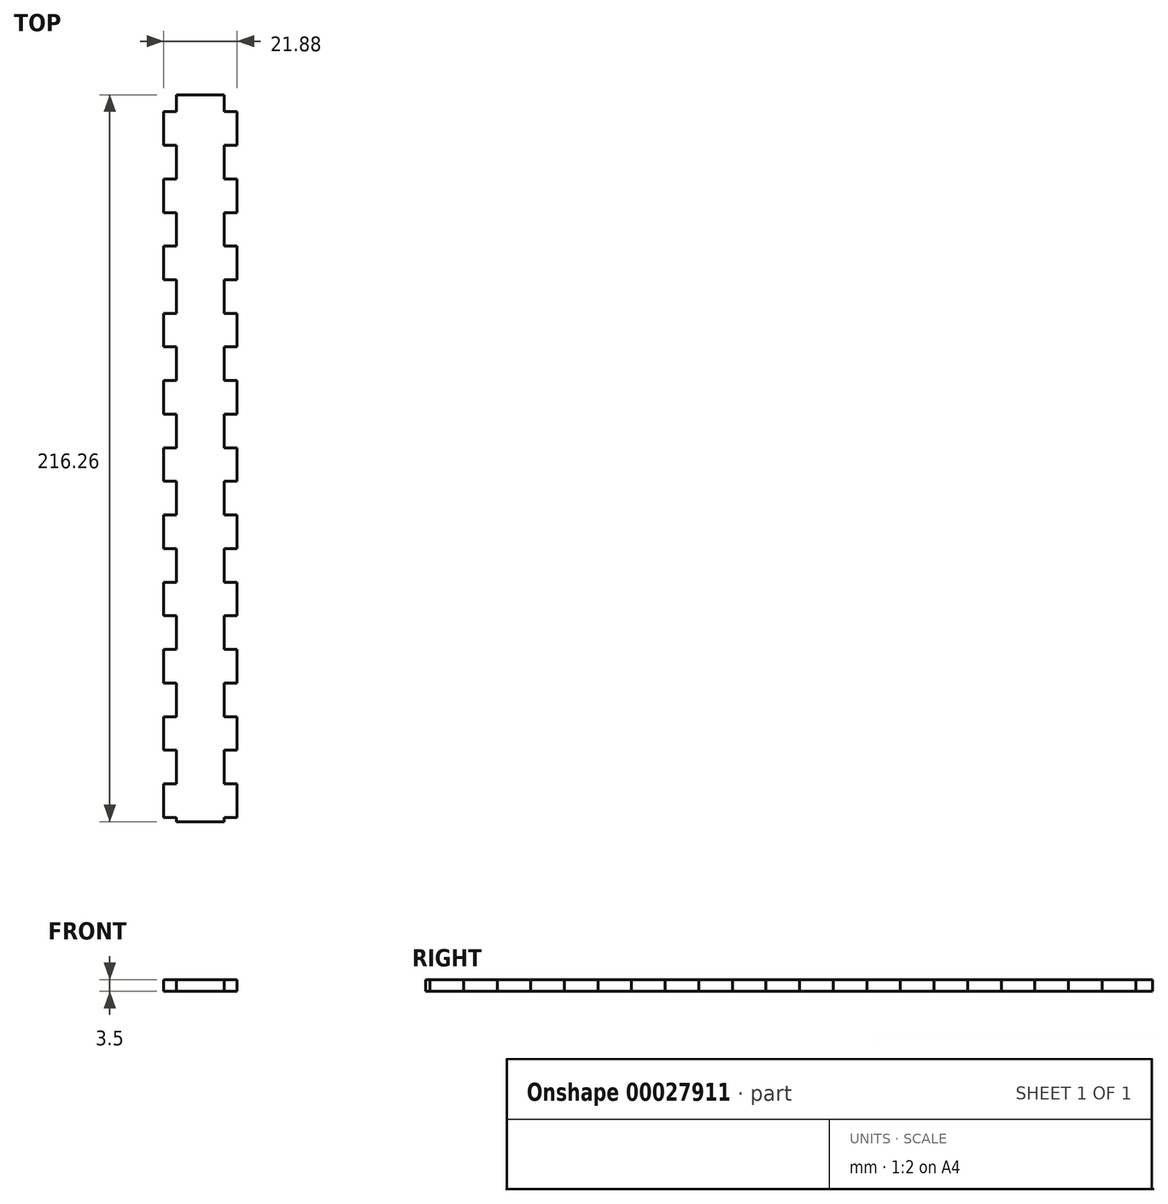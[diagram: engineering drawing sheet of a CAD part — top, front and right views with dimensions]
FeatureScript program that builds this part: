
annotation { "Feature Type Name" : "Feature", "Feature Type Description" : "" }
export const myFeature = defineFeature(function(context is Context, id is Id, definition is map)
    precondition{}
    {
        {
            var Q0;
            Q0=qCreatedBy(makeId("Top.planeOp"),FACE);
            var sketch = newSketch(context, id + "F0", { "sketchPlane" : qUnion([Q0])});
            skLineSegment(sketch, "E0.rect.bottom", {"start": v(7.14, -108.13) * mm, "end": v(-7.14, -108.13) * mm});
            skLineSegment(sketch, "E0.rect.top", {"start": v(7.14, 108.13) * mm, "end": v(-7.14, 108.13) * mm});
            skPoint(sketch, "E0.rect.middle", {"position": v(0, 0) * mm});
            skLineSegment(sketch, "E1", {"start": v(7.14, 108.13) * mm, "end": v(7.14, 103.13) * mm});
            skLineSegment(sketch, "E2.bottom", {"start": v(7.14, 103.13) * mm, "end": v(10.94, 103.13) * mm});
            skLineSegment(sketch, "E2.top", {"start": v(7.14, 93.13) * mm, "end": v(10.94, 93.13) * mm});
            skLineSegment(sketch, "E2.right", {"start": v(10.94, 103.13) * mm, "end": v(10.94, 93.13) * mm});
            skLineSegment(sketch, "E3", {"start": v(7.14, 93.13) * mm, "end": v(7.14, 88.13) * mm});
            skLineSegment(sketch, "E4.0.1.0", {"start": v(7.14, 88.13) * mm, "end": v(7.14, 83.13) * mm});
            skLineSegment(sketch, "E4.0.1.1", {"start": v(7.14, 83.13) * mm, "end": v(10.94, 83.13) * mm});
            skLineSegment(sketch, "E4.0.1.2", {"start": v(10.94, 83.13) * mm, "end": v(10.94, 73.13) * mm});
            skLineSegment(sketch, "E4.0.1.3", {"start": v(7.14, 73.13) * mm, "end": v(10.94, 73.13) * mm});
            skLineSegment(sketch, "E4.0.1.4", {"start": v(7.14, 73.13) * mm, "end": v(7.14, 68.13) * mm});
            skLineSegment(sketch, "E4.0.2.0", {"start": v(7.14, 68.13) * mm, "end": v(7.14, 63.13) * mm});
            skLineSegment(sketch, "E4.0.2.1", {"start": v(7.14, 63.13) * mm, "end": v(10.94, 63.13) * mm});
            skLineSegment(sketch, "E4.0.2.2", {"start": v(10.94, 63.13) * mm, "end": v(10.94, 53.13) * mm});
            skLineSegment(sketch, "E4.0.2.3", {"start": v(7.14, 53.13) * mm, "end": v(10.94, 53.13) * mm});
            skLineSegment(sketch, "E4.0.2.4", {"start": v(7.14, 53.13) * mm, "end": v(7.14, 48.13) * mm});
            skLineSegment(sketch, "E4.0.3.0", {"start": v(7.14, 48.13) * mm, "end": v(7.14, 43.13) * mm});
            skLineSegment(sketch, "E4.0.3.1", {"start": v(7.14, 43.13) * mm, "end": v(10.94, 43.13) * mm});
            skLineSegment(sketch, "E4.0.3.2", {"start": v(10.94, 43.13) * mm, "end": v(10.94, 33.13) * mm});
            skLineSegment(sketch, "E4.0.3.3", {"start": v(7.14, 33.13) * mm, "end": v(10.94, 33.13) * mm});
            skLineSegment(sketch, "E4.0.3.4", {"start": v(7.14, 33.13) * mm, "end": v(7.14, 28.13) * mm});
            skLineSegment(sketch, "E4.0.4.0", {"start": v(7.14, 28.13) * mm, "end": v(7.14, 23.13) * mm});
            skLineSegment(sketch, "E4.0.4.1", {"start": v(7.14, 23.13) * mm, "end": v(10.94, 23.13) * mm});
            skLineSegment(sketch, "E4.0.4.2", {"start": v(10.94, 23.13) * mm, "end": v(10.94, 13.13) * mm});
            skLineSegment(sketch, "E4.0.4.3", {"start": v(7.14, 13.13) * mm, "end": v(10.94, 13.13) * mm});
            skLineSegment(sketch, "E4.0.4.4", {"start": v(7.14, 13.13) * mm, "end": v(7.14, 8.13) * mm});
            skLineSegment(sketch, "E4.0.5.0", {"start": v(7.14, 8.13) * mm, "end": v(7.14, 3.13) * mm});
            skLineSegment(sketch, "E4.0.5.1", {"start": v(7.14, 3.13) * mm, "end": v(10.94, 3.13) * mm});
            skLineSegment(sketch, "E4.0.5.2", {"start": v(10.94, 3.13) * mm, "end": v(10.94, -6.87) * mm});
            skLineSegment(sketch, "E4.0.5.3", {"start": v(7.14, -6.87) * mm, "end": v(10.94, -6.87) * mm});
            skLineSegment(sketch, "E4.0.5.4", {"start": v(7.14, -6.87) * mm, "end": v(7.14, -11.87) * mm});
            skLineSegment(sketch, "E4.0.6.0", {"start": v(7.14, -11.87) * mm, "end": v(7.14, -16.87) * mm});
            skLineSegment(sketch, "E4.0.6.1", {"start": v(7.14, -16.87) * mm, "end": v(10.94, -16.87) * mm});
            skLineSegment(sketch, "E4.0.6.2", {"start": v(10.94, -16.87) * mm, "end": v(10.94, -26.87) * mm});
            skLineSegment(sketch, "E4.0.6.3", {"start": v(7.14, -26.87) * mm, "end": v(10.94, -26.87) * mm});
            skLineSegment(sketch, "E4.0.6.4", {"start": v(7.14, -26.87) * mm, "end": v(7.14, -31.87) * mm});
            skLineSegment(sketch, "E4.0.7.0", {"start": v(7.14, -31.87) * mm, "end": v(7.14, -36.87) * mm});
            skLineSegment(sketch, "E4.0.7.1", {"start": v(7.14, -36.87) * mm, "end": v(10.94, -36.87) * mm});
            skLineSegment(sketch, "E4.0.7.2", {"start": v(10.94, -36.87) * mm, "end": v(10.94, -46.87) * mm});
            skLineSegment(sketch, "E4.0.7.3", {"start": v(7.14, -46.87) * mm, "end": v(10.94, -46.87) * mm});
            skLineSegment(sketch, "E4.0.7.4", {"start": v(7.14, -46.87) * mm, "end": v(7.14, -51.87) * mm});
            skLineSegment(sketch, "E4.0.8.0", {"start": v(7.14, -51.87) * mm, "end": v(7.14, -56.87) * mm});
            skLineSegment(sketch, "E4.0.8.1", {"start": v(7.14, -56.87) * mm, "end": v(10.94, -56.87) * mm});
            skLineSegment(sketch, "E4.0.8.2", {"start": v(10.94, -56.87) * mm, "end": v(10.94, -66.87) * mm});
            skLineSegment(sketch, "E4.0.8.3", {"start": v(7.14, -66.87) * mm, "end": v(10.94, -66.87) * mm});
            skLineSegment(sketch, "E4.0.8.4", {"start": v(7.14, -66.87) * mm, "end": v(7.14, -71.87) * mm});
            skLineSegment(sketch, "E4.0.9.0", {"start": v(7.14, -71.87) * mm, "end": v(7.14, -76.87) * mm});
            skLineSegment(sketch, "E4.0.9.4", {"start": v(7.14, -86.87) * mm, "end": v(7.14, -91.87) * mm});
            skLineSegment(sketch, "E4.0.10.0", {"start": v(7.14, -91.87) * mm, "end": v(7.14, -96.87) * mm});
            skLineSegment(sketch, "E4.0.10.1", {"start": v(7.14, -96.87) * mm, "end": v(10.94, -96.87) * mm});
            skLineSegment(sketch, "E4.0.10.2", {"start": v(10.94, -96.87) * mm, "end": v(10.94, -106.87) * mm});
            skLineSegment(sketch, "E4.0.10.3", {"start": v(7.14, -106.87) * mm, "end": v(10.94, -106.87) * mm});
            skLineSegment(sketch, "E4.0.10.4", {"start": v(7.14, -106.87) * mm, "end": v(7.14, -108.13) * mm});
            skLineSegment(sketch, "E4.0.11.1", {"start": v(7.14, -116.87) * mm, "end": v(10.94, -116.87) * mm});
            skLineSegment(sketch, "E4.0.11.2", {"start": v(10.94, -116.87) * mm, "end": v(10.94, -126.87) * mm});
            skLineSegment(sketch, "E4.0.11.3", {"start": v(7.14, -126.87) * mm, "end": v(10.94, -126.87) * mm});
            skLineSegment(sketch, "E4.0.11.4", {"start": v(7.14, -126.87) * mm, "end": v(7.14, -131.87) * mm});
            skLineSegment(sketch, "E4.direction1", {"start": v(7.14, 103.13) * mm, "end": v(32.14, 103.13) * mm, "construction": true});
            skLineSegment(sketch, "E4.direction2", {"start": v(7.14, 103.13) * mm, "end": v(7.14, 83.13) * mm, "construction": true});
            skLineSegment(sketch, "E5", {"start": v(-7.14, 108.13) * mm, "end": v(-7.14, 103.13) * mm});
            skLineSegment(sketch, "E6.bottom", {"start": v(-7.14, 103.13) * mm, "end": v(-10.94, 103.13) * mm});
            skLineSegment(sketch, "E6.top", {"start": v(-7.14, 93.13) * mm, "end": v(-10.94, 93.13) * mm});
            skLineSegment(sketch, "E6.right", {"start": v(-10.94, 103.13) * mm, "end": v(-10.94, 93.13) * mm});
            skLineSegment(sketch, "E7", {"start": v(-7.14, 93.13) * mm, "end": v(-7.14, 88.13) * mm});
            skLineSegment(sketch, "E8.0.1.0", {"start": v(-7.14, 88.13) * mm, "end": v(-7.14, 83.13) * mm});
            skLineSegment(sketch, "E8.0.1.1", {"start": v(-7.14, 83.13) * mm, "end": v(-10.94, 83.13) * mm});
            skLineSegment(sketch, "E8.0.1.2", {"start": v(-10.94, 83.13) * mm, "end": v(-10.94, 73.13) * mm});
            skLineSegment(sketch, "E8.0.1.3", {"start": v(-7.14, 73.13) * mm, "end": v(-10.94, 73.13) * mm});
            skLineSegment(sketch, "E8.0.1.4", {"start": v(-7.14, 73.13) * mm, "end": v(-7.14, 68.13) * mm});
            skLineSegment(sketch, "E8.0.2.0", {"start": v(-7.14, 68.13) * mm, "end": v(-7.14, 63.13) * mm});
            skLineSegment(sketch, "E8.0.2.1", {"start": v(-7.14, 63.13) * mm, "end": v(-10.94, 63.13) * mm});
            skLineSegment(sketch, "E8.0.2.2", {"start": v(-10.94, 63.13) * mm, "end": v(-10.94, 53.13) * mm});
            skLineSegment(sketch, "E8.0.2.3", {"start": v(-7.14, 53.13) * mm, "end": v(-10.94, 53.13) * mm});
            skLineSegment(sketch, "E8.0.2.4", {"start": v(-7.14, 53.13) * mm, "end": v(-7.14, 48.13) * mm});
            skLineSegment(sketch, "E8.0.3.0", {"start": v(-7.14, 48.13) * mm, "end": v(-7.14, 43.13) * mm});
            skLineSegment(sketch, "E8.0.3.1", {"start": v(-7.14, 43.13) * mm, "end": v(-10.94, 43.13) * mm});
            skLineSegment(sketch, "E8.0.3.2", {"start": v(-10.94, 43.13) * mm, "end": v(-10.94, 33.13) * mm});
            skLineSegment(sketch, "E8.0.3.3", {"start": v(-7.14, 33.13) * mm, "end": v(-10.94, 33.13) * mm});
            skLineSegment(sketch, "E8.0.3.4", {"start": v(-7.14, 33.13) * mm, "end": v(-7.14, 28.13) * mm});
            skLineSegment(sketch, "E8.0.4.0", {"start": v(-7.14, 28.13) * mm, "end": v(-7.14, 23.13) * mm});
            skLineSegment(sketch, "E8.0.4.1", {"start": v(-7.14, 23.13) * mm, "end": v(-10.94, 23.13) * mm});
            skLineSegment(sketch, "E8.0.4.2", {"start": v(-10.94, 23.13) * mm, "end": v(-10.94, 13.13) * mm});
            skLineSegment(sketch, "E8.0.4.3", {"start": v(-7.14, 13.13) * mm, "end": v(-10.94, 13.13) * mm});
            skLineSegment(sketch, "E8.0.4.4", {"start": v(-7.14, 13.13) * mm, "end": v(-7.14, 8.13) * mm});
            skLineSegment(sketch, "E8.0.5.0", {"start": v(-7.14, 8.13) * mm, "end": v(-7.14, 3.13) * mm});
            skLineSegment(sketch, "E8.0.5.1", {"start": v(-7.14, 3.13) * mm, "end": v(-10.94, 3.13) * mm});
            skLineSegment(sketch, "E8.0.5.2", {"start": v(-10.94, 3.13) * mm, "end": v(-10.94, -6.87) * mm});
            skLineSegment(sketch, "E8.0.5.3", {"start": v(-7.14, -6.87) * mm, "end": v(-10.94, -6.87) * mm});
            skLineSegment(sketch, "E8.0.5.4", {"start": v(-7.14, -6.87) * mm, "end": v(-7.14, -11.87) * mm});
            skLineSegment(sketch, "E8.0.6.0", {"start": v(-7.14, -11.87) * mm, "end": v(-7.14, -16.87) * mm});
            skLineSegment(sketch, "E8.0.6.1", {"start": v(-7.14, -16.87) * mm, "end": v(-10.94, -16.87) * mm});
            skLineSegment(sketch, "E8.0.6.2", {"start": v(-10.94, -16.87) * mm, "end": v(-10.94, -26.87) * mm});
            skLineSegment(sketch, "E8.0.6.3", {"start": v(-7.14, -26.87) * mm, "end": v(-10.94, -26.87) * mm});
            skLineSegment(sketch, "E8.0.6.4", {"start": v(-7.14, -26.87) * mm, "end": v(-7.14, -31.87) * mm});
            skLineSegment(sketch, "E8.0.7.0", {"start": v(-7.14, -31.87) * mm, "end": v(-7.14, -36.87) * mm});
            skLineSegment(sketch, "E8.0.7.1", {"start": v(-7.14, -36.87) * mm, "end": v(-10.94, -36.87) * mm});
            skLineSegment(sketch, "E8.0.7.2", {"start": v(-10.94, -36.87) * mm, "end": v(-10.94, -46.87) * mm});
            skLineSegment(sketch, "E8.0.7.3", {"start": v(-7.14, -46.87) * mm, "end": v(-10.94, -46.87) * mm});
            skLineSegment(sketch, "E8.0.7.4", {"start": v(-7.14, -46.87) * mm, "end": v(-7.14, -51.87) * mm});
            skLineSegment(sketch, "E8.0.8.0", {"start": v(-7.14, -51.87) * mm, "end": v(-7.14, -56.87) * mm});
            skLineSegment(sketch, "E8.0.8.1", {"start": v(-7.14, -56.87) * mm, "end": v(-10.94, -56.87) * mm});
            skLineSegment(sketch, "E8.0.8.2", {"start": v(-10.94, -56.87) * mm, "end": v(-10.94, -66.87) * mm});
            skLineSegment(sketch, "E8.0.8.3", {"start": v(-7.14, -66.87) * mm, "end": v(-10.94, -66.87) * mm});
            skLineSegment(sketch, "E8.0.8.4", {"start": v(-7.14, -66.87) * mm, "end": v(-7.14, -71.87) * mm});
            skLineSegment(sketch, "E8.0.9.0", {"start": v(-7.14, -71.87) * mm, "end": v(-7.14, -76.87) * mm});
            skLineSegment(sketch, "E8.0.9.4", {"start": v(-7.14, -86.87) * mm, "end": v(-7.14, -91.87) * mm});
            skLineSegment(sketch, "E8.0.10.0", {"start": v(-7.14, -91.87) * mm, "end": v(-7.14, -96.87) * mm});
            skLineSegment(sketch, "E8.0.10.1", {"start": v(-7.14, -96.87) * mm, "end": v(-10.94, -96.87) * mm});
            skLineSegment(sketch, "E8.0.10.2", {"start": v(-10.94, -96.87) * mm, "end": v(-10.94, -106.87) * mm});
            skLineSegment(sketch, "E8.0.10.3", {"start": v(-7.14, -106.87) * mm, "end": v(-10.94, -106.87) * mm});
            skLineSegment(sketch, "E8.0.10.4", {"start": v(-7.14, -106.87) * mm, "end": v(-7.14, -108.13) * mm});
            skLineSegment(sketch, "E8.0.11.1", {"start": v(-7.14, -116.87) * mm, "end": v(-10.94, -116.87) * mm});
            skLineSegment(sketch, "E8.0.11.2", {"start": v(-10.94, -116.87) * mm, "end": v(-10.94, -126.87) * mm});
            skLineSegment(sketch, "E8.0.11.3", {"start": v(-7.14, -126.87) * mm, "end": v(-10.94, -126.87) * mm});
            skLineSegment(sketch, "E8.0.11.4", {"start": v(-7.14, -126.87) * mm, "end": v(-7.14, -131.87) * mm});
            skLineSegment(sketch, "E8.direction1", {"start": v(-7.14, 103.13) * mm, "end": v(17.86, 103.13) * mm, "construction": true});
            skLineSegment(sketch, "E8.direction2", {"start": v(-7.14, 103.13) * mm, "end": v(-7.14, 83.13) * mm, "construction": true});
            skPoint(sketch, "E9.orphan", {"position": v(-7.14, -111.87) * mm});
            skPoint(sketch, "E10.orphan", {"position": v(7.14, -111.87) * mm});
            skPoint(sketch, "E11.bottom.start.orphan", {"position": v(10.94, -86.87) * mm});
            skPoint(sketch, "E12.bottom.start.orphan", {"position": v(-10.44, -86.87) * mm});
            skLineSegment(sketch, "E13.bottom", {"start": v(7.14, -76.87) * mm, "end": v(10.94, -76.87) * mm});
            skLineSegment(sketch, "E13.top", {"start": v(7.14, -86.87) * mm, "end": v(10.94, -86.87) * mm});
            skLineSegment(sketch, "E13.right", {"start": v(10.94, -76.87) * mm, "end": v(10.94, -86.87) * mm});
            skLineSegment(sketch, "E14.bottom", {"start": v(-7.14, -86.87) * mm, "end": v(-10.94, -86.87) * mm});
            skLineSegment(sketch, "E14.top", {"start": v(-7.14, -76.87) * mm, "end": v(-10.94, -76.87) * mm});
            skLineSegment(sketch, "E14.right", {"start": v(-10.94, -86.87) * mm, "end": v(-10.94, -76.87) * mm});
            skSolve(sketch);
        }
        {
            var Q0;
            Q0 = qSketchRegion(id + "F0", true);
            extrude(context, id + "F1", {"entities" : qUnion([Q0]), "depth" : 3.5 * mm});
        }
    });
